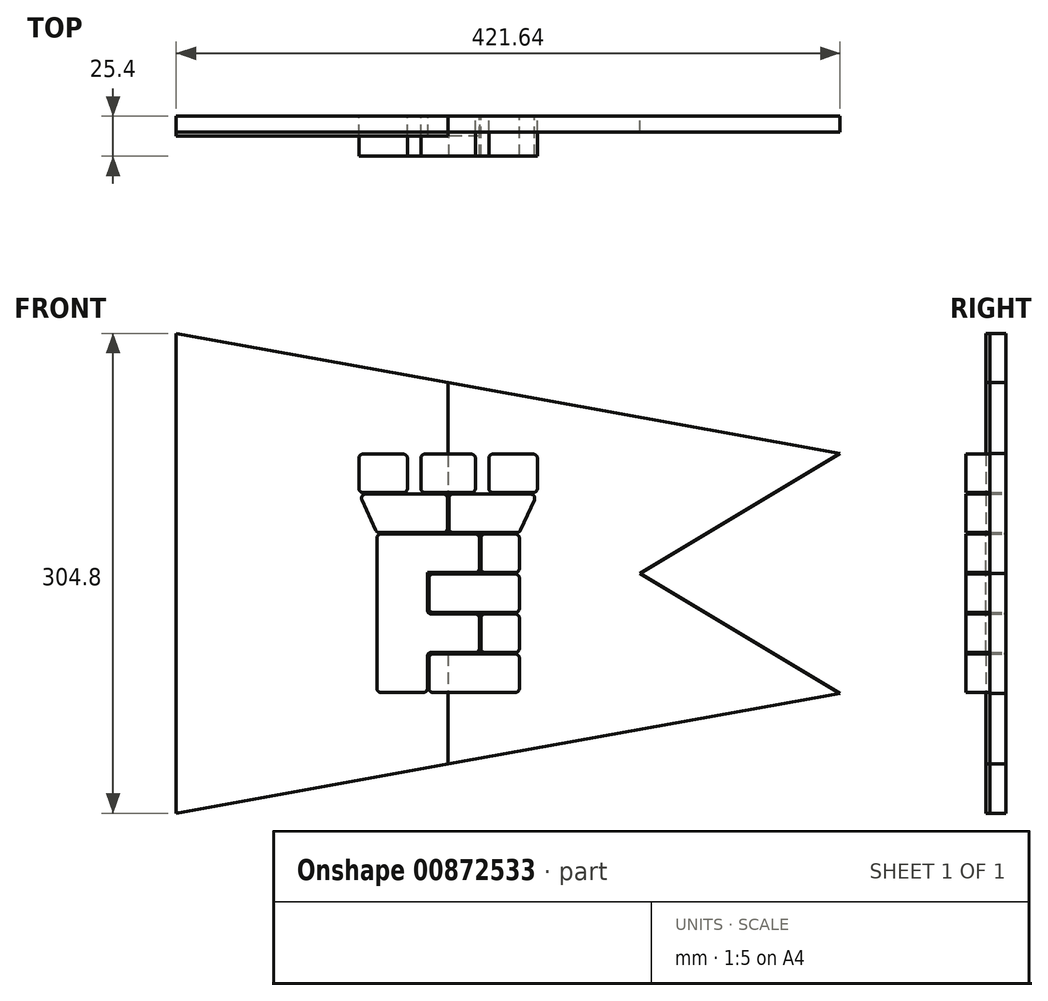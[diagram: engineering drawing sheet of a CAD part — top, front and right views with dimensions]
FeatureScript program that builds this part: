
annotation { "Feature Type Name" : "Feature", "Feature Type Description" : "" }
export const myFeature = defineFeature(function(context is Context, id is Id, definition is map)
    precondition{}
    {
        {
            var Q0;
            Q0=qCreatedBy(makeId("Front.planeOp"),FACE);
            var sketch = newSketch(context, id + "F0", { "sketchPlane" : qUnion([Q0])});
            skLineSegment(sketch, "E0", {"start": v(-45.72, 101.6) * mm, "end": v(-57.15, 127) * mm});
            skLineSegment(sketch, "E1", {"start": v(-57.15, 127) * mm, "end": v(-57.15, 152.4) * mm});
            skLineSegment(sketch, "E2", {"start": v(-57.15, 152.4) * mm, "end": v(-25.4, 152.4) * mm});
            skLineSegment(sketch, "E3", {"start": v(-25.4, 152.4) * mm, "end": v(-25.4, 127) * mm});
            skLineSegment(sketch, "E4", {"start": v(-25.4, 127) * mm, "end": v(-17.78, 127) * mm});
            skLineSegment(sketch, "E5", {"start": v(-17.78, 127) * mm, "end": v(-17.78, 152.4) * mm});
            skLineSegment(sketch, "E6", {"start": v(-17.78, 152.4) * mm, "end": v(17.78, 152.4) * mm});
            skLineSegment(sketch, "E7", {"start": v(17.78, 152.4) * mm, "end": v(17.78, 127) * mm});
            skLineSegment(sketch, "E8", {"start": v(17.78, 127) * mm, "end": v(25.4, 127) * mm});
            skLineSegment(sketch, "E9", {"start": v(25.4, 127) * mm, "end": v(25.4, 152.4) * mm});
            skLineSegment(sketch, "E10", {"start": v(25.4, 152.4) * mm, "end": v(57.15, 152.4) * mm});
            skLineSegment(sketch, "E11", {"start": v(57.15, 152.4) * mm, "end": v(57.15, 127) * mm});
            skLineSegment(sketch, "E12", {"start": v(57.15, 127) * mm, "end": v(45.72, 101.6) * mm});
            skLineSegment(sketch, "E13", {"start": v(-45.72, 101.6) * mm, "end": v(-45.72, 76.2) * mm});
            skLineSegment(sketch, "E14", {"start": v(-45.72, 76.2) * mm, "end": v(-45.72, 50.8) * mm});
            skLineSegment(sketch, "E15", {"start": v(-45.72, 50.8) * mm, "end": v(-45.72, 25.4) * mm});
            skLineSegment(sketch, "E16", {"start": v(-45.72, 25.4) * mm, "end": v(-45.72, 0) * mm});
            skLineSegment(sketch, "E17", {"start": v(45.72, 101.6) * mm, "end": v(45.72, 76.2) * mm});
            skLineSegment(sketch, "E18", {"start": v(45.72, 50.8) * mm, "end": v(45.72, 76.2) * mm});
            skLineSegment(sketch, "E19", {"start": v(45.72, 50.8) * mm, "end": v(45.72, 25.4) * mm});
            skLineSegment(sketch, "E20", {"start": v(45.72, 25.4) * mm, "end": v(45.72, 0) * mm});
            skLineSegment(sketch, "E21", {"start": v(-12.7, 0) * mm, "end": v(-12.7, 25.4) * mm});
            skLineSegment(sketch, "E22", {"start": v(-12.7, 25.4) * mm, "end": v(20.32, 25.4) * mm});
            skLineSegment(sketch, "E23", {"start": v(20.32, 25.4) * mm, "end": v(20.32, 50.8) * mm});
            skLineSegment(sketch, "E24", {"start": v(20.32, 50.8) * mm, "end": v(-12.7, 50.8) * mm});
            skLineSegment(sketch, "E25", {"start": v(-12.7, 50.8) * mm, "end": v(-12.7, 76.2) * mm});
            skLineSegment(sketch, "E26", {"start": v(-12.7, 76.2) * mm, "end": v(20.32, 76.2) * mm});
            skLineSegment(sketch, "E27", {"start": v(20.32, 76.2) * mm, "end": v(20.32, 101.6) * mm});
            skLineSegment(sketch, "E28", {"start": v(20.32, 101.6) * mm, "end": v(-45.72, 101.6) * mm});
            skLineSegment(sketch, "E29", {"start": v(20.32, 25.4) * mm, "end": v(45.72, 25.4) * mm});
            skLineSegment(sketch, "E30", {"start": v(20.32, 50.8) * mm, "end": v(45.72, 50.8) * mm});
            skLineSegment(sketch, "E31", {"start": v(20.32, 76.2) * mm, "end": v(45.72, 76.2) * mm});
            skLineSegment(sketch, "E32", {"start": v(20.32, 101.6) * mm, "end": v(45.72, 101.6) * mm});
            skLineSegment(sketch, "E33", {"start": v(-57.15, 127) * mm, "end": v(-25.4, 127) * mm});
            skLineSegment(sketch, "E34", {"start": v(-17.78, 127) * mm, "end": v(0, 127) * mm});
            skLineSegment(sketch, "E35", {"start": v(0, 127) * mm, "end": v(0, 101.6) * mm});
            skLineSegment(sketch, "E36", {"start": v(0, 127) * mm, "end": v(17.78, 127) * mm});
            skLineSegment(sketch, "E37", {"start": v(25.4, 127) * mm, "end": v(57.15, 127) * mm});
            skLineSegment(sketch, "E38", {"start": v(-45.72, 0) * mm, "end": v(-12.7, 0) * mm});
            skLineSegment(sketch, "E39", {"start": v(-12.7, 0) * mm, "end": v(45.72, 0) * mm});
            skSolve(sketch);
        }
        {
            var Q0;
            {var subQ0=sQuery(id+"F0.wireOp",EDGE,"E13");Q0=makeQuery(id+"F0.imprint","IMPRINT",FACE,{"disambiguationData":[TD([[makeQuery(id+"F0.imprint","IMPRINT",EDGE,{"derivedFrom":subQ0}),1.0]])]});}
            var sketch = newSketch(context, id + "F1", { "sketchPlane" : qUnion([Q0])});
            skLineSegment(sketch, "E40.0", {"start": v(19.81, 79.25) * mm, "end": v(19.81, 98.55) * mm});
            skLineSegment(sketch, "E40.1", {"start": v(-13.2, 76.7) * mm, "end": v(17.27, 76.7) * mm});
            skLineSegment(sketch, "E40.2", {"start": v(-13.2, 52.83) * mm, "end": v(-13.2, 76.7) * mm});
            skLineSegment(sketch, "E40.3", {"start": v(-45.21, 50.8) * mm, "end": v(-45.21, 25.4) * mm});
            skLineSegment(sketch, "E40.4", {"start": v(-45.21, 76.2) * mm, "end": v(-45.21, 50.8) * mm});
            skLineSegment(sketch, "E40.5", {"start": v(-45.21, 98.55) * mm, "end": v(-45.21, 76.2) * mm});
            skLineSegment(sketch, "E40.6", {"start": v(0, 101.1) * mm, "end": v(-42.67, 101.1) * mm});
            skLineSegment(sketch, "E40.7", {"start": v(-45.21, 25.4) * mm, "end": v(-45.21, 3.05) * mm});
            skLineSegment(sketch, "E40.8", {"start": v(-42.67, 0.5) * mm, "end": v(-15.75, 0.5) * mm});
            skLineSegment(sketch, "E40.9", {"start": v(-13.2, 3.05) * mm, "end": v(-13.2, 23.37) * mm});
            skLineSegment(sketch, "E40.10", {"start": v(17.27, 101.1) * mm, "end": v(0, 101.1) * mm});
            skLineSegment(sketch, "E40.11", {"start": v(-10.67, 25.9) * mm, "end": v(17.27, 25.9) * mm});
            skLineSegment(sketch, "E40.12", {"start": v(19.81, 28.45) * mm, "end": v(19.81, 47.75) * mm});
            skLineSegment(sketch, "E40.13", {"start": v(17.27, 50.3) * mm, "end": v(-10.67, 50.3) * mm});
            skLineSegment(sketch, "E41.0", {"start": v(15.24, 24.9) * mm, "end": v(-9.65, 24.9) * mm});
            skLineSegment(sketch, "E41.1", {"start": v(42.67, 24.9) * mm, "end": v(15.24, 24.9) * mm});
            skLineSegment(sketch, "E41.2", {"start": v(-12.2, 22.35) * mm, "end": v(-12.2, 3.05) * mm});
            skLineSegment(sketch, "E41.3", {"start": v(-9.65, 0.5) * mm, "end": v(42.67, 0.5) * mm});
            skLineSegment(sketch, "E41.4", {"start": v(45.21, 3.05) * mm, "end": v(45.21, 22.35) * mm});
            skLineSegment(sketch, "E42.0", {"start": v(42.67, 50.3) * mm, "end": v(23.37, 50.3) * mm});
            skLineSegment(sketch, "E42.1", {"start": v(45.21, 28.45) * mm, "end": v(45.21, 47.75) * mm});
            skLineSegment(sketch, "E42.2", {"start": v(23.37, 25.9) * mm, "end": v(42.67, 25.9) * mm});
            skLineSegment(sketch, "E42.3", {"start": v(20.83, 47.75) * mm, "end": v(20.83, 28.45) * mm});
            skLineSegment(sketch, "E43.0", {"start": v(45.21, 53.85) * mm, "end": v(45.21, 73.15) * mm});
            skLineSegment(sketch, "E43.1", {"start": v(25.4, 75.7) * mm, "end": v(-9.65, 75.7) * mm});
            skLineSegment(sketch, "E43.2", {"start": v(-12.2, 73.15) * mm, "end": v(-12.2, 53.85) * mm});
            skLineSegment(sketch, "E43.3", {"start": v(42.67, 75.7) * mm, "end": v(25.4, 75.7) * mm});
            skLineSegment(sketch, "E43.4", {"start": v(-9.65, 51.3) * mm, "end": v(15.24, 51.3) * mm});
            skLineSegment(sketch, "E43.5", {"start": v(15.24, 51.3) * mm, "end": v(42.67, 51.3) * mm});
            skLineSegment(sketch, "E44.0", {"start": v(42.67, 101.1) * mm, "end": v(23.37, 101.1) * mm});
            skLineSegment(sketch, "E44.1", {"start": v(45.21, 79.25) * mm, "end": v(45.21, 98.55) * mm});
            skLineSegment(sketch, "E44.2", {"start": v(23.37, 76.7) * mm, "end": v(42.67, 76.7) * mm});
            skLineSegment(sketch, "E44.3", {"start": v(20.83, 98.55) * mm, "end": v(20.83, 79.25) * mm});
            skLineSegment(sketch, "E45.0", {"start": v(46.07, 103.6) * mm, "end": v(54.75, 122.9) * mm});
            skLineSegment(sketch, "E45.1", {"start": v(25.4, 102.1) * mm, "end": v(43.75, 102.1) * mm});
            skLineSegment(sketch, "E45.2", {"start": v(25.4, 126.5) * mm, "end": v(15.24, 126.5) * mm});
            skLineSegment(sketch, "E45.3", {"start": v(15.24, 126.5) * mm, "end": v(3.05, 126.5) * mm});
            skLineSegment(sketch, "E45.4", {"start": v(0.5, 123.95) * mm, "end": v(0.5, 104.65) * mm});
            skLineSegment(sketch, "E45.5", {"start": v(52.44, 126.5) * mm, "end": v(25.4, 126.5) * mm});
            skLineSegment(sketch, "E45.6", {"start": v(3.05, 102.1) * mm, "end": v(25.4, 102.1) * mm});
            skLineSegment(sketch, "E46.0", {"start": v(-0.5, 104.65) * mm, "end": v(-0.5, 123.95) * mm});
            skLineSegment(sketch, "E46.1", {"start": v(-15.24, 126.5) * mm, "end": v(-25.4, 126.5) * mm});
            skLineSegment(sketch, "E46.2", {"start": v(-25.4, 126.5) * mm, "end": v(-52.44, 126.5) * mm});
            skLineSegment(sketch, "E46.3", {"start": v(-3.05, 126.5) * mm, "end": v(-15.24, 126.5) * mm});
            skLineSegment(sketch, "E46.4", {"start": v(-54.75, 122.9) * mm, "end": v(-46.07, 103.6) * mm});
            skLineSegment(sketch, "E46.5", {"start": v(-43.75, 102.1) * mm, "end": v(-3.05, 102.1) * mm});
            skLineSegment(sketch, "E47.0", {"start": v(-56.64, 149.35) * mm, "end": v(-56.64, 130.05) * mm});
            skLineSegment(sketch, "E47.1", {"start": v(-28.45, 151.9) * mm, "end": v(-54.1, 151.9) * mm});
            skLineSegment(sketch, "E47.2", {"start": v(-25.9, 130.05) * mm, "end": v(-25.9, 149.35) * mm});
            skLineSegment(sketch, "E47.3", {"start": v(-54.1, 127.5) * mm, "end": v(-28.45, 127.5) * mm});
            skLineSegment(sketch, "E48.0", {"start": v(-14.73, 127.5) * mm, "end": v(0, 127.5) * mm});
            skLineSegment(sketch, "E48.1", {"start": v(-17.27, 149.35) * mm, "end": v(-17.27, 130.05) * mm});
            skLineSegment(sketch, "E48.2", {"start": v(0, 127.5) * mm, "end": v(14.73, 127.5) * mm});
            skLineSegment(sketch, "E48.3", {"start": v(17.27, 130.05) * mm, "end": v(17.27, 149.35) * mm});
            skLineSegment(sketch, "E48.4", {"start": v(14.73, 151.9) * mm, "end": v(-14.73, 151.9) * mm});
            skLineSegment(sketch, "E49.0", {"start": v(25.9, 149.35) * mm, "end": v(25.9, 130.05) * mm});
            skLineSegment(sketch, "E49.1", {"start": v(54.1, 151.9) * mm, "end": v(28.45, 151.9) * mm});
            skLineSegment(sketch, "E49.2", {"start": v(56.64, 130.05) * mm, "end": v(56.64, 149.35) * mm});
            skLineSegment(sketch, "E49.3", {"start": v(28.45, 127.5) * mm, "end": v(54.1, 127.5) * mm});
            skPoint(sketch, "E50.visualSharp", {"position": v(-56.64, 151.9) * mm});
            skArc(sketch, "E50.filletArc", {"start": v(-54.1, 151.9) * mm, "mid": v(-55.9, 151.15) * mm, "end": v(-56.64, 149.35) * mm});
            skPoint(sketch, "E51.visualSharp", {"position": v(-56.64, 127.5) * mm});
            skArc(sketch, "E51.filletArc", {"start": v(-56.64, 130.05) * mm, "mid": v(-55.9, 128.25) * mm, "end": v(-54.1, 127.5) * mm});
            skPoint(sketch, "E52.visualSharp", {"position": v(-25.9, 127.5) * mm});
            skArc(sketch, "E52.filletArc", {"start": v(-28.45, 127.5) * mm, "mid": v(-26.65, 128.25) * mm, "end": v(-25.9, 130.05) * mm});
            skPoint(sketch, "E53.visualSharp", {"position": v(-25.9, 151.9) * mm});
            skArc(sketch, "E53.filletArc", {"start": v(-25.9, 149.35) * mm, "mid": v(-26.65, 151.15) * mm, "end": v(-28.45, 151.9) * mm});
            skPoint(sketch, "E54.visualSharp", {"position": v(-17.27, 151.9) * mm});
            skArc(sketch, "E54.filletArc", {"start": v(-14.73, 151.9) * mm, "mid": v(-16.53, 151.15) * mm, "end": v(-17.27, 149.35) * mm});
            skPoint(sketch, "E55.visualSharp", {"position": v(-17.27, 127.5) * mm});
            skArc(sketch, "E55.filletArc", {"start": v(-17.27, 130.05) * mm, "mid": v(-16.53, 128.25) * mm, "end": v(-14.73, 127.5) * mm});
            skPoint(sketch, "E56.visualSharp", {"position": v(-56.36, 126.5) * mm});
            skArc(sketch, "E56.filletArc", {"start": v(-52.44, 126.5) * mm, "mid": v(-54.57, 125.33) * mm, "end": v(-54.75, 122.9) * mm});
            skPoint(sketch, "E57.visualSharp", {"position": v(-45.4, 102.1) * mm});
            skArc(sketch, "E57.filletArc", {"start": v(-46.07, 103.6) * mm, "mid": v(-45.13, 102.52) * mm, "end": v(-43.75, 102.1) * mm});
            skPoint(sketch, "E58.visualSharp", {"position": v(-0.5, 126.5) * mm});
            skArc(sketch, "E58.filletArc", {"start": v(-0.5, 123.95) * mm, "mid": v(-1.25, 125.75) * mm, "end": v(-3.05, 126.5) * mm});
            skPoint(sketch, "E59.visualSharp", {"position": v(-0.5, 102.1) * mm});
            skArc(sketch, "E59.filletArc", {"start": v(-3.05, 102.1) * mm, "mid": v(-1.25, 102.85) * mm, "end": v(-0.5, 104.65) * mm});
            skPoint(sketch, "E60.visualSharp", {"position": v(0.5, 102.1) * mm});
            skArc(sketch, "E60.filletArc", {"start": v(0.5, 104.65) * mm, "mid": v(1.25, 102.85) * mm, "end": v(3.05, 102.1) * mm});
            skPoint(sketch, "E61.visualSharp", {"position": v(0.5, 126.5) * mm});
            skArc(sketch, "E61.filletArc", {"start": v(3.05, 126.5) * mm, "mid": v(1.25, 125.75) * mm, "end": v(0.5, 123.95) * mm});
            skPoint(sketch, "E62.visualSharp", {"position": v(17.27, 151.9) * mm});
            skArc(sketch, "E62.filletArc", {"start": v(17.27, 149.35) * mm, "mid": v(16.53, 151.15) * mm, "end": v(14.73, 151.9) * mm});
            skPoint(sketch, "E63.visualSharp", {"position": v(17.27, 127.5) * mm});
            skArc(sketch, "E63.filletArc", {"start": v(14.73, 127.5) * mm, "mid": v(16.53, 128.25) * mm, "end": v(17.27, 130.05) * mm});
            skPoint(sketch, "E64.visualSharp", {"position": v(25.9, 127.5) * mm});
            skArc(sketch, "E64.filletArc", {"start": v(25.9, 130.05) * mm, "mid": v(26.65, 128.25) * mm, "end": v(28.45, 127.5) * mm});
            skPoint(sketch, "E65.visualSharp", {"position": v(25.9, 151.9) * mm});
            skArc(sketch, "E65.filletArc", {"start": v(28.45, 151.9) * mm, "mid": v(26.65, 151.15) * mm, "end": v(25.9, 149.35) * mm});
            skPoint(sketch, "E66.visualSharp", {"position": v(56.64, 151.9) * mm});
            skArc(sketch, "E66.filletArc", {"start": v(56.64, 149.35) * mm, "mid": v(55.9, 151.15) * mm, "end": v(54.1, 151.9) * mm});
            skPoint(sketch, "E67.visualSharp", {"position": v(56.64, 127.5) * mm});
            skArc(sketch, "E67.filletArc", {"start": v(54.1, 127.5) * mm, "mid": v(55.9, 128.25) * mm, "end": v(56.64, 130.05) * mm});
            skPoint(sketch, "E68.visualSharp", {"position": v(56.36, 126.5) * mm});
            skArc(sketch, "E68.filletArc", {"start": v(54.75, 122.9) * mm, "mid": v(54.57, 125.33) * mm, "end": v(52.44, 126.5) * mm});
            skPoint(sketch, "E69.visualSharp", {"position": v(45.4, 102.1) * mm});
            skArc(sketch, "E69.filletArc", {"start": v(43.75, 102.1) * mm, "mid": v(45.13, 102.52) * mm, "end": v(46.07, 103.6) * mm});
            skPoint(sketch, "E70.visualSharp", {"position": v(45.21, 101.1) * mm});
            skArc(sketch, "E70.filletArc", {"start": v(45.21, 98.55) * mm, "mid": v(44.47, 100.35) * mm, "end": v(42.67, 101.1) * mm});
            skPoint(sketch, "E71.visualSharp", {"position": v(20.83, 101.1) * mm});
            skArc(sketch, "E71.filletArc", {"start": v(23.37, 101.1) * mm, "mid": v(21.57, 100.35) * mm, "end": v(20.83, 98.55) * mm});
            skPoint(sketch, "E72.visualSharp", {"position": v(19.81, 101.1) * mm});
            skArc(sketch, "E72.filletArc", {"start": v(19.81, 98.55) * mm, "mid": v(19.07, 100.35) * mm, "end": v(17.27, 101.1) * mm});
            skPoint(sketch, "E73.visualSharp", {"position": v(20.83, 76.7) * mm});
            skArc(sketch, "E73.filletArc", {"start": v(20.83, 79.25) * mm, "mid": v(21.57, 77.45) * mm, "end": v(23.37, 76.7) * mm});
            skPoint(sketch, "E74.visualSharp", {"position": v(19.81, 76.7) * mm});
            skArc(sketch, "E74.filletArc", {"start": v(17.27, 76.7) * mm, "mid": v(19.07, 77.45) * mm, "end": v(19.81, 79.25) * mm});
            skPoint(sketch, "E75.visualSharp", {"position": v(45.21, 76.7) * mm});
            skArc(sketch, "E75.filletArc", {"start": v(42.67, 76.7) * mm, "mid": v(44.47, 77.45) * mm, "end": v(45.21, 79.25) * mm});
            skPoint(sketch, "E76.visualSharp", {"position": v(45.21, 75.7) * mm});
            skArc(sketch, "E76.filletArc", {"start": v(45.21, 73.15) * mm, "mid": v(44.47, 74.95) * mm, "end": v(42.67, 75.7) * mm});
            skPoint(sketch, "E77.visualSharp", {"position": v(-12.2, 75.7) * mm});
            skArc(sketch, "E77.filletArc", {"start": v(-9.65, 75.7) * mm, "mid": v(-11.45, 74.95) * mm, "end": v(-12.2, 73.15) * mm});
            skPoint(sketch, "E78.visualSharp", {"position": v(-12.2, 51.3) * mm});
            skArc(sketch, "E78.filletArc", {"start": v(-12.2, 53.85) * mm, "mid": v(-11.45, 52.05) * mm, "end": v(-9.65, 51.3) * mm});
            skPoint(sketch, "E79.visualSharp", {"position": v(45.21, 51.3) * mm});
            skArc(sketch, "E79.filletArc", {"start": v(42.67, 51.3) * mm, "mid": v(44.47, 52.05) * mm, "end": v(45.21, 53.85) * mm});
            skPoint(sketch, "E80.visualSharp", {"position": v(19.81, 50.3) * mm});
            skArc(sketch, "E80.filletArc", {"start": v(19.81, 47.75) * mm, "mid": v(19.07, 49.55) * mm, "end": v(17.27, 50.3) * mm});
            skPoint(sketch, "E81.visualSharp", {"position": v(20.83, 50.3) * mm});
            skArc(sketch, "E81.filletArc", {"start": v(23.37, 50.3) * mm, "mid": v(21.57, 49.55) * mm, "end": v(20.83, 47.75) * mm});
            skPoint(sketch, "E82.visualSharp", {"position": v(45.21, 50.3) * mm});
            skArc(sketch, "E82.filletArc", {"start": v(45.21, 47.75) * mm, "mid": v(44.47, 49.55) * mm, "end": v(42.67, 50.3) * mm});
            skPoint(sketch, "E83.visualSharp", {"position": v(20.83, 25.9) * mm});
            skArc(sketch, "E83.filletArc", {"start": v(20.83, 28.45) * mm, "mid": v(21.57, 26.65) * mm, "end": v(23.37, 25.9) * mm});
            skPoint(sketch, "E84.visualSharp", {"position": v(19.81, 25.9) * mm});
            skArc(sketch, "E84.filletArc", {"start": v(17.27, 25.9) * mm, "mid": v(19.07, 26.65) * mm, "end": v(19.81, 28.45) * mm});
            skPoint(sketch, "E85.visualSharp", {"position": v(-12.2, 24.9) * mm});
            skArc(sketch, "E85.filletArc", {"start": v(-9.65, 24.9) * mm, "mid": v(-11.45, 24.15) * mm, "end": v(-12.2, 22.35) * mm});
            skPoint(sketch, "E86.visualSharp", {"position": v(-12.2, 0.5) * mm});
            skArc(sketch, "E86.filletArc", {"start": v(-12.2, 3.05) * mm, "mid": v(-11.45, 1.25) * mm, "end": v(-9.65, 0.5) * mm});
            skPoint(sketch, "E87.visualSharp", {"position": v(45.21, 0.5) * mm});
            skArc(sketch, "E87.filletArc", {"start": v(42.67, 0.5) * mm, "mid": v(44.47, 1.25) * mm, "end": v(45.21, 3.05) * mm});
            skPoint(sketch, "E88.visualSharp", {"position": v(45.21, 24.9) * mm});
            skArc(sketch, "E88.filletArc", {"start": v(45.21, 22.35) * mm, "mid": v(44.47, 24.15) * mm, "end": v(42.67, 24.9) * mm});
            skPoint(sketch, "E89.visualSharp", {"position": v(45.21, 25.9) * mm});
            skArc(sketch, "E89.filletArc", {"start": v(42.67, 25.9) * mm, "mid": v(44.47, 26.65) * mm, "end": v(45.21, 28.45) * mm});
            skPoint(sketch, "E90.visualSharp", {"position": v(-13.2, 25.9) * mm});
            skArc(sketch, "E90.filletArc", {"start": v(-10.67, 25.9) * mm, "mid": v(-12.46, 25.16) * mm, "end": v(-13.2, 23.37) * mm});
            skPoint(sketch, "E91.visualSharp", {"position": v(-13.2, 0.5) * mm});
            skArc(sketch, "E91.filletArc", {"start": v(-15.75, 0.5) * mm, "mid": v(-13.95, 1.25) * mm, "end": v(-13.2, 3.05) * mm});
            skPoint(sketch, "E92.visualSharp", {"position": v(-13.2, 50.3) * mm});
            skArc(sketch, "E92.filletArc", {"start": v(-13.2, 52.83) * mm, "mid": v(-12.46, 51.04) * mm, "end": v(-10.67, 50.3) * mm});
            skPoint(sketch, "E93.visualSharp", {"position": v(-45.21, 0.5) * mm});
            skArc(sketch, "E93.filletArc", {"start": v(-45.21, 3.05) * mm, "mid": v(-44.47, 1.25) * mm, "end": v(-42.67, 0.5) * mm});
            skPoint(sketch, "E94.visualSharp", {"position": v(-45.21, 101.1) * mm});
            skArc(sketch, "E94.filletArc", {"start": v(-42.67, 101.1) * mm, "mid": v(-44.47, 100.35) * mm, "end": v(-45.21, 98.55) * mm});
            skSolve(sketch);
        }
        {
            var Q0;
            Q0 = qSketchRegion(id + "F1", true);
            extrude(context, id + "F2", {"entities" : qUnion([Q0]), "depth" : 25.4 * mm, "offsetDistance" : 25.4 * mm});
        }
        {
            var Q0;
            Q0=qCreatedBy(makeId("Front.planeOp"),FACE);
            var sketch = newSketch(context, id + "F3", { "sketchPlane" : qUnion([Q0])});
            skLineSegment(sketch, "E95", {"start": v(-172.72, 228.6) * mm, "end": v(-172.72, -76.2) * mm});
            skLineSegment(sketch, "E96", {"start": v(-172.72, -76.2) * mm, "end": v(248.92, 0) * mm});
            skLineSegment(sketch, "E97", {"start": v(248.92, 0) * mm, "end": v(121.92, 76.2) * mm});
            skLineSegment(sketch, "E98", {"start": v(121.92, 76.2) * mm, "end": v(248.92, 152.4) * mm});
            skLineSegment(sketch, "E99", {"start": v(248.92, 152.4) * mm, "end": v(-172.72, 228.6) * mm});
            skLineSegment(sketch, "E100", {"start": v(-172.72, 76.2) * mm, "end": v(121.92, 76.2) * mm, "construction": true});
            skSolve(sketch);
        }
        {
            var Q0;
            Q0=makeQuery(id+"F3.imprint","IMPRINT",FACE,{"disambiguationData":[TD([[makeQuery(id+"F3.imprint","IMPRINT",EDGE,{"derivedFrom":sQuery(id+"F3.wireOp",EDGE,"E95")}),1.0]])]});
            var sketch = newSketch(context, id + "F4", { "sketchPlane" : qUnion([Q0])});
            skLineSegment(sketch, "E101.10.2", {"start": v(-172.72, 228.6) * mm, "end": v(-172.72, -76.2) * mm});
            skLineSegment(sketch, "E102.2", {"start": v(20.32, 25.4) * mm, "end": v(20.32, 50.8) * mm});
            skLineSegment(sketch, "E102.3", {"start": v(20.32, 50.8) * mm, "end": v(-12.7, 50.8) * mm});
            skLineSegment(sketch, "E102.4", {"start": v(-12.7, 50.8) * mm, "end": v(-12.7, 76.2) * mm});
            skLineSegment(sketch, "E102.5", {"start": v(20.32, 76.2) * mm, "end": v(20.32, 101.6) * mm});
            skLineSegment(sketch, "E102.6", {"start": v(-12.7, 76.2) * mm, "end": v(20.32, 76.2) * mm});
            skLineSegment(sketch, "E102.7", {"start": v(0, 127) * mm, "end": v(0, 101.6) * mm});
            skLineSegment(sketch, "E103", {"start": v(20.32, 101.6) * mm, "end": v(0, 101.6) * mm});
            skLineSegment(sketch, "E104", {"start": v(-172.72, -76.2) * mm, "end": v(0, -44.99) * mm});
            skLineSegment(sketch, "E105", {"start": v(0, 197.39) * mm, "end": v(-172.72, 228.6) * mm});
            skLineSegment(sketch, "E106", {"start": v(0, 127) * mm, "end": v(0, 197.39) * mm});
            skLineSegment(sketch, "E107", {"start": v(0, 25.4) * mm, "end": v(0, -44.99) * mm});
            skLineSegment(sketch, "E108", {"start": v(20.32, 25.4) * mm, "end": v(0, 25.4) * mm});
            skSolve(sketch);
        }
        {
            var Q0;
            Q0 = qSketchRegion(id + "F4", true);
            extrude(context, id + "F5", {"entities" : qUnion([Q0]), "depth" : 12.7 * mm, "offsetDistance" : 25.4 * mm});
        }
        {
            var Q0;
            Q0=makeQuery(id+"F3.imprint","IMPRINT",FACE,{"disambiguationData":[TD([[makeQuery(id+"F3.imprint","IMPRINT",EDGE,{"derivedFrom":sQuery(id+"F3.wireOp",EDGE,"E95")}),1.0]])]});
            extrude(context, id + "F6", {"entities" : qUnion([Q0]), "depth" : 10.16 * mm, "offsetDistance" : 25.4 * mm});
        }
    });
